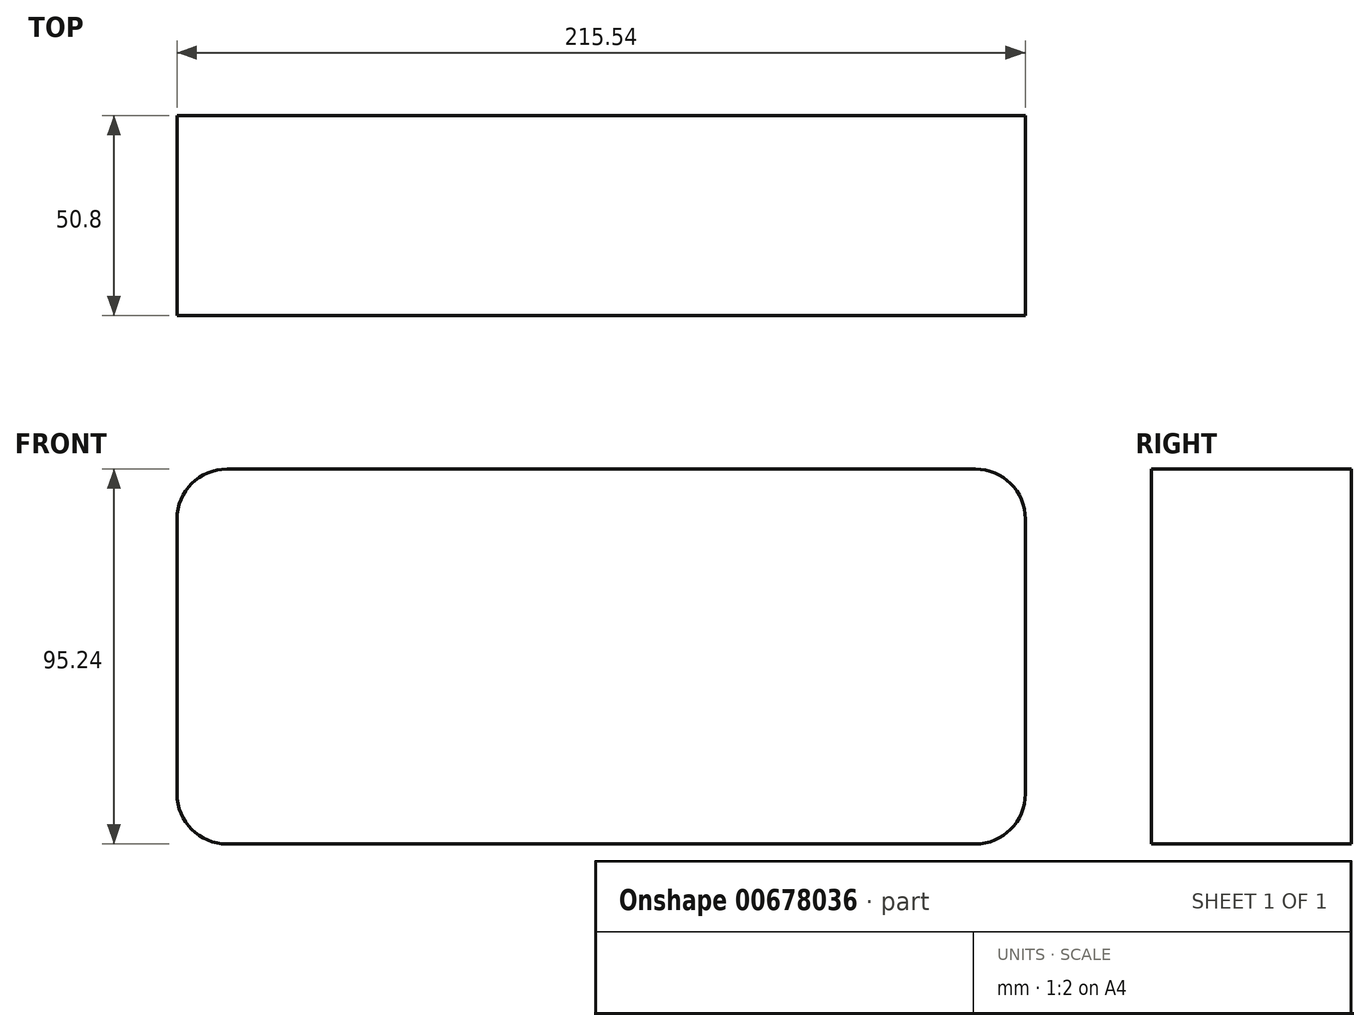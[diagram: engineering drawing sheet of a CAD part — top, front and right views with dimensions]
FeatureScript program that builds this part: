
annotation { "Feature Type Name" : "Feature", "Feature Type Description" : "" }
export const myFeature = defineFeature(function(context is Context, id is Id, definition is map)
    precondition{}
    {
        {
            var Q0;
            Q0=qCreatedBy(makeId("Front.planeOp"),FACE);
            var sketch = newSketch(context, id + "F0", { "sketchPlane" : qUnion([Q0])});
            skCircle(sketch, "E0", {"center": v(0, 0) * mm, "radius": 32.38 * mm});
            skLineSegment(sketch, "E1.bottom", {"start": v(-95.07, 47.63) * mm, "end": v(95.07, 47.63) * mm});
            skLineSegment(sketch, "E1.top", {"start": v(-95.07, -47.63) * mm, "end": v(95.07, -47.63) * mm});
            skLineSegment(sketch, "E1.left", {"start": v(-107.77, 34.93) * mm, "end": v(-107.77, -34.93) * mm});
            skLineSegment(sketch, "E1.right", {"start": v(107.77, 34.93) * mm, "end": v(107.77, -34.93) * mm});
            skPoint(sketch, "E2.visualSharp", {"position": v(-107.77, 47.63) * mm});
            skArc(sketch, "E2.filletArc", {"start": v(-95.07, 47.63) * mm, "mid": v(-104.05, 43.9) * mm, "end": v(-107.77, 34.93) * mm});
            skPoint(sketch, "E3.visualSharp", {"position": v(107.77, 47.63) * mm});
            skArc(sketch, "E3.filletArc", {"start": v(107.77, 34.93) * mm, "mid": v(104.05, 43.9) * mm, "end": v(95.07, 47.63) * mm});
            skPoint(sketch, "E4.visualSharp", {"position": v(107.77, -47.63) * mm});
            skArc(sketch, "E4.filletArc", {"start": v(95.07, -47.63) * mm, "mid": v(104.05, -43.9) * mm, "end": v(107.77, -34.93) * mm});
            skPoint(sketch, "E5.visualSharp", {"position": v(-107.77, -47.63) * mm});
            skArc(sketch, "E5.filletArc", {"start": v(-107.77, -34.93) * mm, "mid": v(-104.05, -43.9) * mm, "end": v(-95.07, -47.63) * mm});
            skCircle(sketch, "E6", {"center": v(-55.37, 0) * mm, "radius": 20.32 * mm});
            skCircle(sketch, "E7", {"center": v(55.37, 0) * mm, "radius": 20.32 * mm});
            skSolve(sketch);
        }
        {
            var Q0;
            Q0=makeQuery(id+"F0.imprint","IMPRINT",FACE,{"disambiguationData":[TD([[makeQuery(id+"F0.imprint","IMPRINT",EDGE,{"derivedFrom":sQuery(id+"F0.wireOp",EDGE,"E0")}),-1.0]])]});
            var Q1;
            Q1=makeQuery(id+"F0.imprint","IMPRINT",FACE,{"disambiguationData":[TD([[makeQuery(id+"F0.imprint","IMPRINT",EDGE,{"derivedFrom":sQuery(id+"F0.wireOp",EDGE,"E6")}),1.0]])]});
            var Q2;
            Q2=makeQuery(id+"F0.imprint","IMPRINT",FACE,{"disambiguationData":[TD([[makeQuery(id+"F0.imprint","IMPRINT",EDGE,{"derivedFrom":sQuery(id+"F0.wireOp",EDGE,"E0")}),1.0]])]});
            var Q3;
            Q3=makeQuery(id+"F0.imprint","IMPRINT",FACE,{"disambiguationData":[TD([[makeQuery(id+"F0.imprint","IMPRINT",EDGE,{"derivedFrom":sQuery(id+"F0.wireOp",EDGE,"E7")}),1.0]])]});
            extrude(context, id + "F1", {"entities" : qUnion([Q0, Q1, Q2, Q3]), "depth" : 50.8 * mm, "offsetDistance" : 25.4 * mm});
        }
    });
